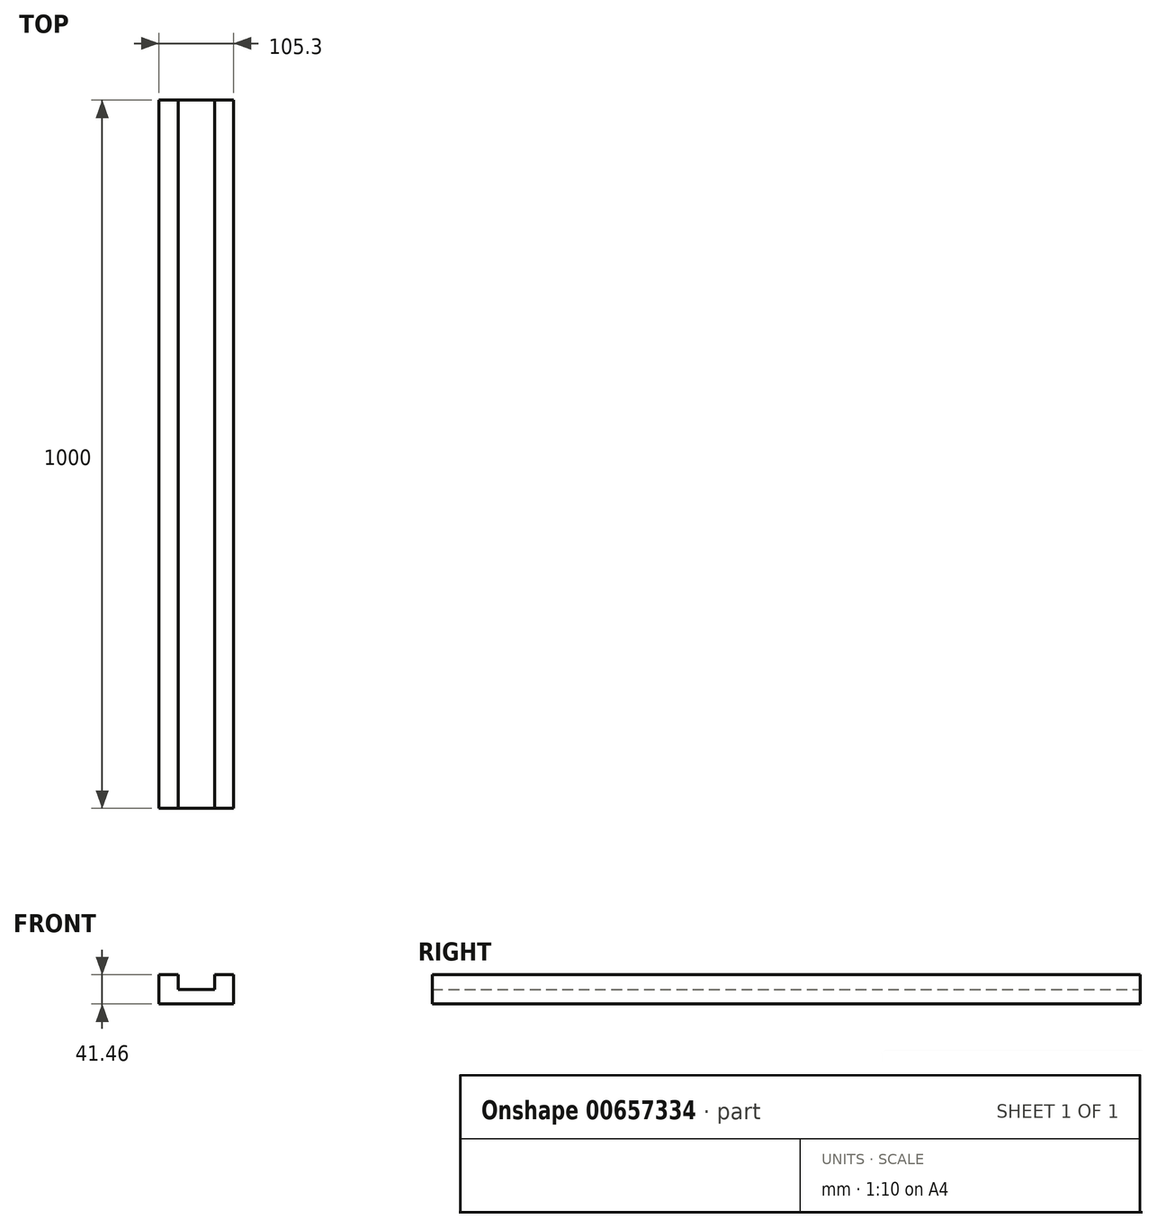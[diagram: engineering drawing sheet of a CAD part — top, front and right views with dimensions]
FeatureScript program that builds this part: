
annotation { "Feature Type Name" : "Feature", "Feature Type Description" : "" }
export const myFeature = defineFeature(function(context is Context, id is Id, definition is map)
    precondition{}
    {
        {
            var Q0;
            Q0=qCreatedBy(makeId("Front.planeOp"),FACE);
            var sketch = newSketch(context, id + "F0", { "sketchPlane" : qUnion([Q0])});
            skLineSegment(sketch, "E0.bottom", {"start": v(52.65, -20.73) * mm, "end": v(-52.65, -20.73) * mm});
            skLineSegment(sketch, "E0.top", {"start": v(52.65, 20.73) * mm, "end": v(-52.65, 20.73) * mm});
            skLineSegment(sketch, "E0.left", {"start": v(52.65, -20.73) * mm, "end": v(52.65, 20.73) * mm});
            skLineSegment(sketch, "E0.right", {"start": v(-52.65, -20.73) * mm, "end": v(-52.65, 20.73) * mm});
            skPoint(sketch, "E0.middle", {"position": v(0, 0) * mm});
            skLineSegment(sketch, "E1.bottom", {"start": v(-25.53, 20.73) * mm, "end": v(25.87, 20.73) * mm});
            skLineSegment(sketch, "E1.top", {"start": v(-25.53, 0) * mm, "end": v(25.87, 0) * mm});
            skLineSegment(sketch, "E1.left", {"start": v(-25.53, 20.73) * mm, "end": v(-25.53, 0) * mm});
            skLineSegment(sketch, "E1.right", {"start": v(25.87, 20.73) * mm, "end": v(25.87, 0) * mm});
            skSolve(sketch);
        }
        {
            var Q0;
            Q0=makeQuery(id+"F0.imprint","IMPRINT",FACE,{"disambiguationData":[TD([[makeQuery(id+"F0.imprint","IMPRINT",EDGE,{"derivedFrom":sQuery(id+"F0.wireOp",EDGE,"E0.bottom")}),-1.0]])]});
            extrude(context, id + "F1", {"entities" : qUnion([Q0]), "depth" : 1000 * mm, "offsetDistance" : 25.4 * mm});
        }
    });
